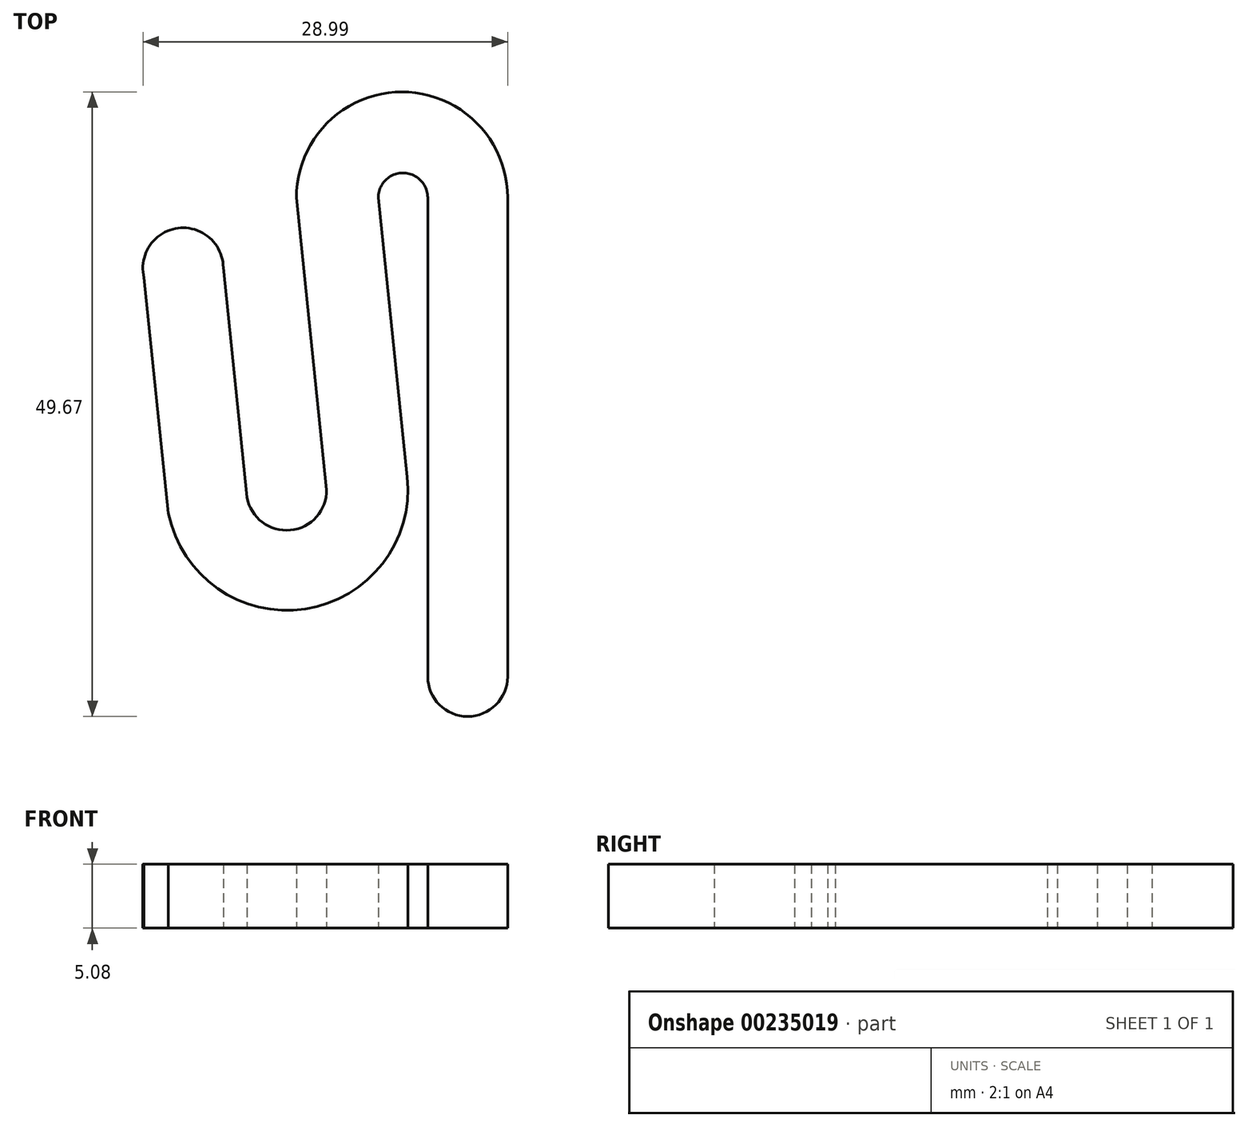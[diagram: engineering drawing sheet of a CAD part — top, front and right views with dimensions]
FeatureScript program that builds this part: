
annotation { "Feature Type Name" : "Feature", "Feature Type Description" : "" }
export const myFeature = defineFeature(function(context is Context, id is Id, definition is map)
    precondition{}
    {
        {
            var Q0;
            Q0=qCreatedBy(makeId("Top.planeOp"),FACE);
            var sketch = newSketch(context, id + "F0", { "sketchPlane" : qUnion([Q0])});
            skLineSegment(sketch, "E0.bottom", {"start": v(3.72, -12.18) * mm, "end": v(3.72, -12.18) * mm});
            skLineSegment(sketch, "E0.left", {"start": v(0.55, -9) * mm, "end": v(0.55, 29.1) * mm});
            skLineSegment(sketch, "E0.right", {"start": v(6.9, -9) * mm, "end": v(6.9, 29.1) * mm});
            skPoint(sketch, "E1.visualSharp", {"position": v(0.55, -12.18) * mm});
            skArc(sketch, "E1.filletArc", {"start": v(0.55, -9) * mm, "mid": v(1.48, -11.25) * mm, "end": v(3.72, -12.18) * mm});
            skPoint(sketch, "E2.visualSharp", {"position": v(6.9, -12.18) * mm});
            skArc(sketch, "E2.filletArc", {"start": v(3.72, -12.18) * mm, "mid": v(5.97, -11.25) * mm, "end": v(6.9, -9) * mm});
            skLineSegment(sketch, "E3", {"start": v(-3.37, 29.07) * mm, "end": v(-1.07, 6.87) * mm});
            skLineSegment(sketch, "E4", {"start": v(-9.9, 29.07) * mm, "end": v(-7.5, 5.88) * mm});
            skLineSegment(sketch, "E5", {"start": v(-15.76, 24.11) * mm, "end": v(-13.81, 5.26) * mm});
            skLineSegment(sketch, "E6", {"start": v(-22.1, 23.6) * mm, "end": v(-20.06, 3.98) * mm});
            skArc(sketch, "E7", {"start": v(-1.07, 6.87) * mm, "mid": v(-9.2, -3.63) * mm, "end": v(-20.06, 3.98) * mm});
            skArc(sketch, "E8", {"start": v(-15.7, 23.52) * mm, "mid": v(-19.3, 26.66) * mm, "end": v(-22, 22.73) * mm});
            skArc(sketch, "E9", {"start": v(-13.81, 5.26) * mm, "mid": v(-10.37, 2.64) * mm, "end": v(-7.5, 5.88) * mm});
            skArc(sketch, "E10", {"start": v(0.55, 29.1) * mm, "mid": v(-1.43, 31.05) * mm, "end": v(-3.37, 29.07) * mm});
            skArc(sketch, "E11", {"start": v(6.9, 29.1) * mm, "mid": v(-1.5, 37.49) * mm, "end": v(-9.9, 29.07) * mm});
            skSolve(sketch);
        }
        {
            var Q0;
            Q0 = qSketchRegion(id + "F0", true);
            extrude(context, id + "F1", {"entities" : qUnion([Q0]), "depth" : 5.08 * mm});
        }
    });
